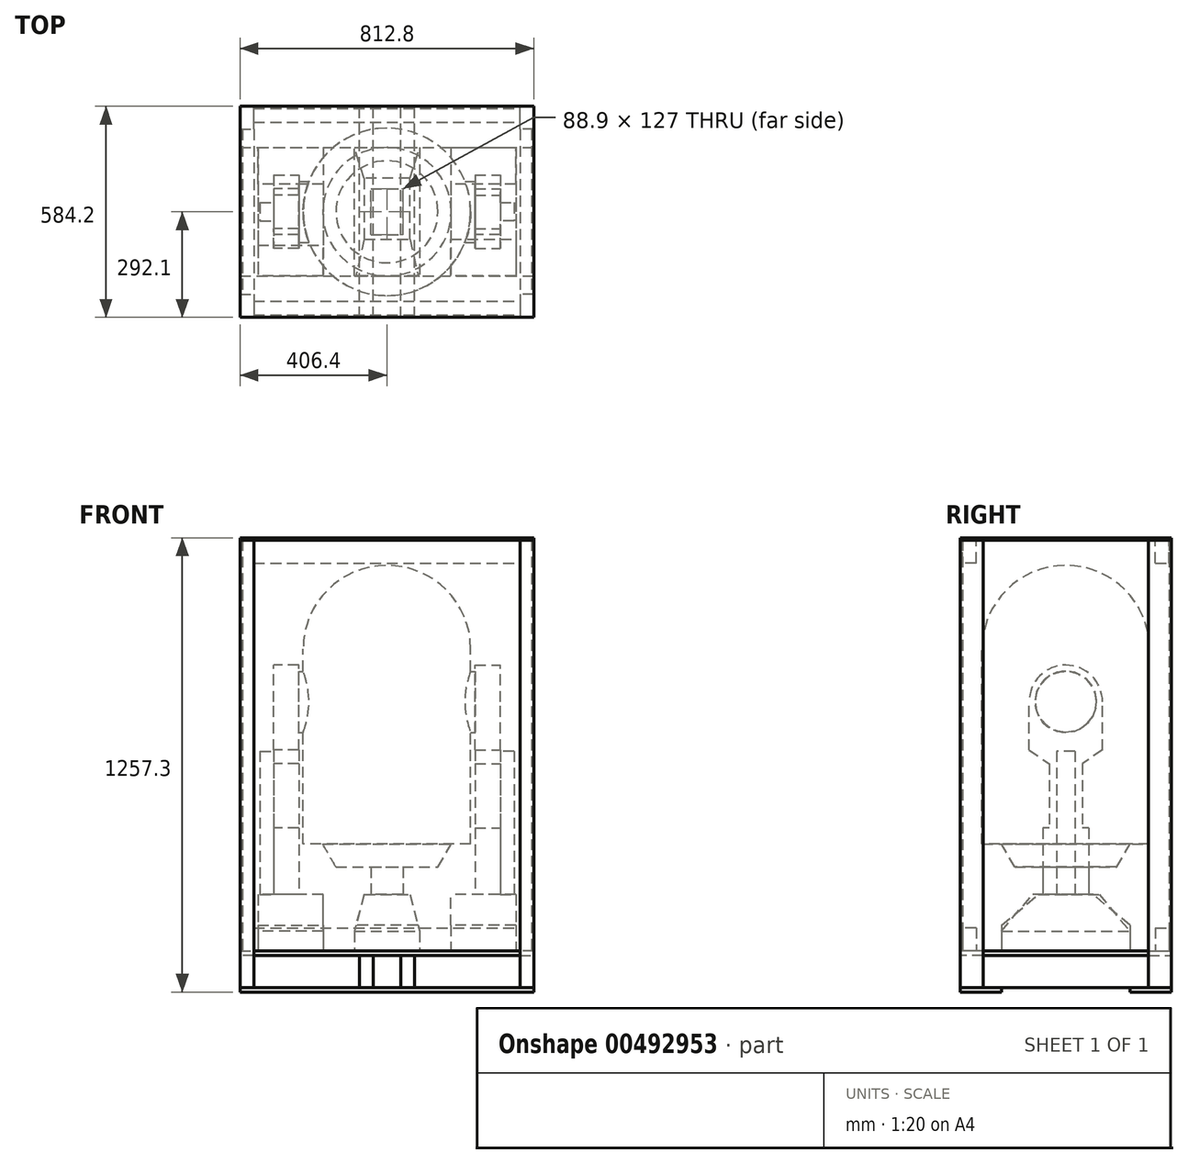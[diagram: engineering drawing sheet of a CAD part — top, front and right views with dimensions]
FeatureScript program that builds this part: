
annotation { "Feature Type Name" : "Feature", "Feature Type Description" : "" }
export const myFeature = defineFeature(function(context is Context, id is Id, definition is map)
    precondition{}
    {
        {
            var Q0;
            Q0=qCreatedBy(makeId("Top.planeOp"),FACE);
            var sketch = newSketch(context, id + "F0", { "sketchPlane" : qUnion([Q0])});
            skCircle(sketch, "E0", {"center": v(0, 0) * mm, "radius": 231.78 * mm});
            skLineSegment(sketch, "E1.bottom", {"start": v(243.68, 84.58) * mm, "end": v(215.8, 84.58) * mm});
            skLineSegment(sketch, "E1.top", {"start": v(243.68, -84.58) * mm, "end": v(215.8, -84.58) * mm});
            skLineSegment(sketch, "E1.left", {"start": v(243.68, 84.58) * mm, "end": v(243.68, -84.58) * mm});
            skLineSegment(sketch, "E1.right", {"start": v(-243.68, 84.58) * mm, "end": v(-243.68, -84.58) * mm});
            skLineSegment(sketch, "E2.bottom", {"start": v(313.53, 101.6) * mm, "end": v(243.68, 101.6) * mm});
            skLineSegment(sketch, "E2.top", {"start": v(313.53, -101.6) * mm, "end": v(243.68, -101.6) * mm});
            skLineSegment(sketch, "E2.left", {"start": v(313.53, 101.6) * mm, "end": v(313.53, -101.6) * mm});
            skLineSegment(sketch, "E2.right", {"start": v(243.68, 101.6) * mm, "end": v(243.68, -101.6) * mm});
            skPoint(sketch, "E2.middle", {"position": v(278.6, 0) * mm});
            skLineSegment(sketch, "E3.bottom", {"start": v(338.93, -50.8) * mm, "end": v(313.53, -50.8) * mm});
            skLineSegment(sketch, "E3.top", {"start": v(338.93, 50.8) * mm, "end": v(313.53, 50.8) * mm});
            skLineSegment(sketch, "E3.left", {"start": v(338.93, -50.8) * mm, "end": v(338.93, 50.8) * mm});
            skLineSegment(sketch, "E3.right", {"start": v(313.53, -50.8) * mm, "end": v(313.53, 50.8) * mm});
            skPoint(sketch, "E3.middle", {"position": v(326.23, 0) * mm});
            skLineSegment(sketch, "E4.trimOffspring", {"start": v(-215.8, 84.58) * mm, "end": v(-243.68, 84.58) * mm});
            skLineSegment(sketch, "E5.trimOffspring", {"start": v(-215.8, -84.58) * mm, "end": v(-243.68, -84.58) * mm});
            skLineSegment(sketch, "E6.MirrorCS", {"start": v(-243.68, 101.6) * mm, "end": v(-243.68, -101.6) * mm});
            skLineSegment(sketch, "E7.MirrorCS", {"start": v(-313.53, 101.6) * mm, "end": v(-243.68, 101.6) * mm});
            skLineSegment(sketch, "E8.MirrorCS", {"start": v(-313.53, -101.6) * mm, "end": v(-243.68, -101.6) * mm});
            skLineSegment(sketch, "E9.MirrorCS", {"start": v(-313.53, 101.6) * mm, "end": v(-313.53, -101.6) * mm});
            skLineSegment(sketch, "E10.MirrorCS", {"start": v(-338.93, -50.8) * mm, "end": v(-313.53, -50.8) * mm});
            skLineSegment(sketch, "E11.MirrorCS", {"start": v(-338.93, -50.8) * mm, "end": v(-338.93, 50.8) * mm});
            skLineSegment(sketch, "E12.MirrorCS", {"start": v(-338.93, 50.8) * mm, "end": v(-313.53, 50.8) * mm});
            skLineSegment(sketch, "E13", {"start": v(0, 0) * mm, "end": v(0, 231.78) * mm});
            skLineSegment(sketch, "E14", {"start": v(0, 0) * mm, "end": v(0, -231.78) * mm});
            skLineSegment(sketch, "E15", {"start": v(313.53, 0) * mm, "end": v(243.68, 0) * mm});
            skLineSegment(sketch, "E16", {"start": v(-243.68, 0) * mm, "end": v(-313.53, 0) * mm});
            skSolve(sketch);
        }
        {
            var Q0;
            {var subQ0=sQuery(id+"F0.wireOp",EDGE,"E0");var subQ1=makeQuery(id+"F0.imprint","INTERSECT",VERTEX,{"derivedFrom":[subQ0,sQuery(id+"F0.wireOp",EDGE,"E1.bottom")]});Q0=makeQuery(id+"F0.imprint","IMPRINT",FACE,{"disambiguationData":[TD([[makeQuery(id+"F0.imprint","IMPRINT",EDGE,{"disambiguationData":[TD([[subQ1,-1.0]])],"derivedFrom":subQ0}),1.0]])]});}
            var Q1;
            {var subQ3=sQuery(id+"F0.wireOp",EDGE,"E13");Q1=makeQuery(id+"F0.imprint","IMPRINT",FACE,{"disambiguationData":[TD([[makeQuery(id+"F0.imprint","IMPRINT",EDGE,{"derivedFrom":subQ3}),1.0]])]});}
            extrude(context, id + "F1", {"entities" : qUnion([Q0, Q1]), "oppositeDirection" : true, "depth" : 539.75 * mm});
        }
        {
            var Q0;
            {var subQ0=sQuery(id+"F0.wireOp",EDGE,"E13");Q0=makeQuery(id+"F0.imprint","IMPRINT",FACE,{"disambiguationData":[TD([[makeQuery(id+"F0.imprint","IMPRINT",EDGE,{"derivedFrom":subQ0}),-1.0]])]});}
            var Q1;
            Q1=sQuery(id+"F0.wireOp",EDGE,"E14");
            revolve(context, id + "F2", {"operationType" : NewBodyOperationType.ADD, "entities" : qUnion([Q0]), "axis" : qUnion([Q1]), "revolveType" : RevolveType.ONE_DIRECTION, "angle" : 180 * degree});
        }
        {
            var Q0;
            {var subQ2=sQuery(id+"F0.wireOp",EDGE,"E2.top");Q0=makeQuery(id+"F0.imprint","IMPRINT",FACE,{"disambiguationData":[TD([[makeQuery(id+"F0.imprint","IMPRINT",EDGE,{"derivedFrom":subQ2}),-1.0]])]});}
            var Q1;
            {var subQ2=sQuery(id+"F0.wireOp",EDGE,"E2.bottom");Q1=makeQuery(id+"F0.imprint","IMPRINT",FACE,{"disambiguationData":[TD([[makeQuery(id+"F0.imprint","IMPRINT",EDGE,{"derivedFrom":subQ2}),1.0]])]});}
            extrude(context, id + "F3", {"entities" : qUnion([Q0, Q1]), "oppositeDirection" : true, "depth" : 714.38 * mm, "hasSecondDirection" : true, "secondDirectionOppositeDirection" : true, "secondDirectionDepth" : 146.05 * mm});
        }
        {
            var Q0;
            Q0=makeQuery(id+"F3.opExtrude","CAP_FACE",FACE,{"disambiguationData":[OSD([sQuery(id+"F0.wireOp",EDGE,"E2.bottom"),sQuery(id+"F0.wireOp",EDGE,"E2.top"),sQuery(id+"F0.wireOp",EDGE,"E2.left"),sQuery(id+"F0.wireOp",EDGE,"E2.right"),sQuery(id+"F0.wireOp",EDGE,"E3.right")])],"isStart":true});
            var sketch = newSketch(context, id + "F4", { "sketchPlane" : qUnion([Q0])});
            skLineSegment(sketch, "E17", {"start": v(313.53, 0) * mm, "end": v(243.68, 0) * mm});
            skSolve(sketch);
        }
        {
            var Q0;
            {var subQ0=sQuery(id+"F4.wireOp",EDGE,"E17");Q0=makeQuery(id+"F4.imprint","IMPRINT",FACE,{"disambiguationData":[TD([[makeQuery(id+"F4.imprint","IMPRINT",EDGE,{"derivedFrom":subQ0}),1.0]])]});}
            var Q1;
            Q1=sQuery(id+"F4.wireOp",EDGE,"E17");
            revolve(context, id + "F5", {"operationType" : NewBodyOperationType.ADD, "entities" : qUnion([Q0]), "axis" : qUnion([Q1]), "revolveType" : RevolveType.FULL});
        }
        {
            var Q0;
            {var subQ0=sQuery(id+"F0.wireOp",EDGE,"E3.right");var subQ1=sQuery(id+"F0.wireOp",EDGE,"E2.left");Q0=makeQuery(id+"F5.boolean.opBoolean","MERGE",FACE,{"derivedFrom":[makeQuery(id+"F3.opExtrude","SWEPT_FACE",FACE,{"disambiguationData":[OSD([subQ1,subQ0])]}),makeQuery(id+"F5.opRevolve","SWEPT_FACE",FACE,{"disambiguationData":[OSD([subQ1,subQ0])]})]});}
            var sketch = newSketch(context, id + "F6", { "sketchPlane" : qUnion([Q0])});
            skCircle(sketch, "E18", {"center": v(0, -146.05) * mm, "radius": 84.58 * mm});
            skLineSegment(sketch, "E19.bottom", {"start": v(46.04, -317.5) * mm, "end": v(-46.04, -317.5) * mm, "construction": true});
            skLineSegment(sketch, "E19.left", {"start": v(46.04, -317.5) * mm, "end": v(46.04, -495.3) * mm});
            skLineSegment(sketch, "E19.right", {"start": v(-46.04, -317.5) * mm, "end": v(-46.04, -495.3) * mm});
            skPoint(sketch, "E19.middle", {"position": v(0, -406.4) * mm});
            skLineSegment(sketch, "E20", {"start": v(-101.6, -279.4) * mm, "end": v(-46.04, -317.5) * mm});
            skLineSegment(sketch, "E21", {"start": v(101.6, -279.4) * mm, "end": v(46.04, -317.5) * mm});
            skLineSegment(sketch, "E22.bottom", {"start": v(63.5, -495.3) * mm, "end": v(46.04, -495.3) * mm});
            skLineSegment(sketch, "E22.top", {"start": v(63.5, -714.38) * mm, "end": v(-63.5, -714.38) * mm});
            skLineSegment(sketch, "E22.left", {"start": v(63.5, -495.3) * mm, "end": v(63.5, -714.38) * mm});
            skLineSegment(sketch, "E22.right", {"start": v(-63.5, -495.3) * mm, "end": v(-63.5, -714.38) * mm});
            skPoint(sketch, "E22.middle", {"position": v(0, -604.84) * mm});
            skLineSegment(sketch, "E23.trimOffspring", {"start": v(-46.04, -495.3) * mm, "end": v(-63.5, -495.3) * mm});
            skSolve(sketch);
        }
        {
            var Q0;
            Q0=makeQuery(id+"F6.imprint","IMPRINT",FACE,{"disambiguationData":[TD([[makeQuery(id+"F6.imprint","IMPRINT",EDGE,{"derivedFrom":sQuery(id+"F6.wireOp",EDGE,"E19.left")}),1.0]])]});
            var Q1;
            Q1=makeQuery(id+"F6.imprint","IMPRINT",FACE,{"disambiguationData":[TD([[makeQuery(id+"F6.imprint","IMPRINT",EDGE,{"derivedFrom":sQuery(id+"F6.wireOp",EDGE,"E19.right")}),-1.0]])]});
            var Q2;
            {var subQ0=sQuery(id+"F0.wireOp",EDGE,"E2.right");Q2=makeQuery(id+"F5.boolean.opBoolean","MERGE",FACE,{"derivedFrom":[makeQuery(id+"F3.opExtrude","SWEPT_FACE",FACE,{"disambiguationData":[OSD([subQ0])]}),makeQuery(id+"F5.opRevolve","SWEPT_FACE",FACE,{"disambiguationData":[OSD([subQ0])]})]});}
            extrude(context, id + "F7", {"entities" : qUnion([Q0, Q1]), "operationType" : NewBodyOperationType.REMOVE, "endBound" : BoundingType.UP_TO_SURFACE, "oppositeDirection" : true, "endBoundEntityFace" : qUnion([Q2]), "depth" : 25.4 * mm});
        }
        {
            var Q0;
            Q0=makeQuery(id+"F6.imprint","IMPRINT",FACE,{"disambiguationData":[TD([[makeQuery(id+"F6.imprint","IMPRINT",EDGE,{"derivedFrom":sQuery(id+"F6.wireOp",EDGE,"E18")}),-1.0]])]});
            var sketch = newSketch(context, id + "F8", { "sketchPlane" : qUnion([Q0])});
            skLineSegment(sketch, "E24.bottom", {"start": v(25.4, -282.58) * mm, "end": v(-25.4, -282.58) * mm});
            skLineSegment(sketch, "E24.top", {"start": v(25.4, -714.38) * mm, "end": v(-25.4, -714.38) * mm});
            skLineSegment(sketch, "E24.left", {"start": v(25.4, -282.58) * mm, "end": v(25.4, -714.38) * mm});
            skLineSegment(sketch, "E24.right", {"start": v(-25.4, -282.58) * mm, "end": v(-25.4, -714.38) * mm});
            skPoint(sketch, "E24.middle", {"position": v(0, -498.48) * mm});
            skSolve(sketch);
        }
        {
            var Q0;
            Q0=makeQuery(id+"F8.imprint","IMPRINT",FACE,{"disambiguationData":[TD([[makeQuery(id+"F8.imprint","IMPRINT",EDGE,{"derivedFrom":sQuery(id+"F8.wireOp",EDGE,"E24.bottom")}),1.0]])]});
            extrude(context, id + "F9", {"entities" : qUnion([Q0]), "operationType" : NewBodyOperationType.ADD, "depth" : 38.1 * mm});
        }
        {
            var Q0;
            Q0=makeQuery(id+"F3.opExtrude","SWEPT_BODY",BODY,{"disambiguationData":[OSD([sQuery(id+"F0.wireOp",EDGE,"E2.bottom"),sQuery(id+"F0.wireOp",EDGE,"E2.top"),sQuery(id+"F0.wireOp",EDGE,"E2.left"),sQuery(id+"F0.wireOp",EDGE,"E2.right"),sQuery(id+"F0.wireOp",EDGE,"E3.right")])]});
            var Q1;
            Q1=qCreatedBy(makeId("Right.planeOp"),FACE);
            mirror(context, id + "F10", {"entities" : qUnion([Q0]), "mirrorPlane" : qUnion([Q1])});
        }
        {
            var Q0;
            Q0=makeQuery(id+"F6.imprint","IMPRINT",FACE,{"disambiguationData":[TD([[makeQuery(id+"F6.imprint","IMPRINT",EDGE,{"derivedFrom":sQuery(id+"F6.wireOp",EDGE,"E18")}),1.0]])]});
            var Q1;
            Q1=sQuery(id+"F6.wireOp",EDGE,"E18");
            var Q2;
            {var subQ0=sQuery(id+"F0.wireOp",EDGE,"E3.right");var subQ1=sQuery(id+"F0.wireOp",EDGE,"E2.left");Q2=makeQuery(id+"F10.opPattern","COPY",FACE,{"derivedFrom":makeQuery(id+"F5.boolean.opBoolean","MERGE",FACE,{"derivedFrom":[makeQuery(id+"F3.opExtrude","SWEPT_FACE",FACE,{"disambiguationData":[OSD([subQ1,subQ0])]}),makeQuery(id+"F5.opRevolve","SWEPT_FACE",FACE,{"disambiguationData":[OSD([subQ1,subQ0])]})]}),"instanceName":"1"});}
            extrude(context, id + "F11", {"entities" : qUnion([Q0]), "operationType" : NewBodyOperationType.ADD, "surfaceEntities" : qUnion([Q1]), "endBound" : BoundingType.UP_TO_SURFACE, "oppositeDirection" : true, "endBoundEntityFace" : qUnion([Q2]), "depth" : 25.4 * mm});
        }
        {
            var Q0;
            Q0=makeQuery(id+"F1.opExtrude","CAP_FACE",FACE,{"disambiguationData":[OSD([sQuery(id+"F0.wireOp",EDGE,"E0")])],"isStart":false});
            var sketch = newSketch(context, id + "F12", { "sketchPlane" : qUnion([Q0])});
            skCircle(sketch, "E25", {"center": v(0, 0) * mm, "radius": 177.8 * mm});
            skSolve(sketch);
        }
        {
            var Q0;
            Q0=makeQuery(id+"F12.imprint","IMPRINT",FACE,{"disambiguationData":[TD([[makeQuery(id+"F12.imprint","IMPRINT",EDGE,{"derivedFrom":sQuery(id+"F12.wireOp",EDGE,"E25")}),1.0]])]});
            extrude(context, id + "F13", {"entities" : qUnion([Q0]), "operationType" : NewBodyOperationType.ADD, "depth" : 63.5 * mm});
        }
        {
            var Q0;
            Q0=makeQuery(id+"F13.opExtrude","CAP_EDGE",EDGE,{"disambiguationData":[OSD([sQuery(id+"F12.wireOp",EDGE,"E25")])],"isStart":false});
            chamfer(context, id + "F14", {"entities" : qUnion([Q0]), "chamferType" : ChamferType.OFFSET_ANGLE, "width" : 63.5 * mm, "oppositeDirection" : true, "angle" : 30 * degree, "tangentPropagation" : true});
        }
        {
            var Q0;
            Q0=qCreatedBy(makeId("Top.planeOp"),FACE);
            cPlane(context, id + "F15", {"entities" : qUnion([Q0]), "cplaneType" : CPlaneType.OFFSET, "offset" : 835.02 * mm, "oppositeDirection" : true, "width" : 152.4 * mm, "height" : 152.4 * mm});
        }
        {
            var Q0;
            Q0=qCreatedBy(id+"F15.planeOp",FACE);
            var sketch = newSketch(context, id + "F16", { "sketchPlane" : qUnion([Q0])});
            skLineSegment(sketch, "E26.bottom", {"start": v(-90.49, 177.8) * mm, "end": v(90.49, 177.8) * mm});
            skLineSegment(sketch, "E26.top", {"start": v(-90.49, -177.8) * mm, "end": v(90.49, -177.8) * mm});
            skLineSegment(sketch, "E26.left", {"start": v(-90.49, 177.8) * mm, "end": v(-90.49, -177.8) * mm});
            skLineSegment(sketch, "E26.right", {"start": v(90.49, 177.8) * mm, "end": v(90.49, -177.8) * mm});
            skPoint(sketch, "E26.middle", {"position": v(0, 0) * mm});
            skLineSegment(sketch, "E27.1.0.0", {"start": v(176.21, -177.8) * mm, "end": v(357.19, -177.8) * mm});
            skLineSegment(sketch, "E27.1.0.1", {"start": v(176.21, 177.8) * mm, "end": v(176.21, -177.8) * mm});
            skLineSegment(sketch, "E27.1.0.2", {"start": v(357.19, 177.8) * mm, "end": v(357.19, -177.8) * mm});
            skLineSegment(sketch, "E27.1.0.3", {"start": v(176.21, 177.8) * mm, "end": v(357.19, 177.8) * mm});
            skLineSegment(sketch, "E27.direction1", {"start": v(-90.49, -177.8) * mm, "end": v(176.21, -177.8) * mm, "construction": true});
            skLineSegment(sketch, "E28", {"start": v(266.7, -177.8) * mm, "end": v(266.7, 177.8) * mm, "construction": true});
            skLineSegment(sketch, "E29", {"start": v(0, -177.8) * mm, "end": v(0, 177.8) * mm, "construction": true});
            skLineSegment(sketch, "E30.MirrorCS", {"start": v(-176.21, 177.8) * mm, "end": v(-176.21, -177.8) * mm});
            skLineSegment(sketch, "E31.MirrorCS", {"start": v(-176.21, -177.8) * mm, "end": v(-357.19, -177.8) * mm});
            skLineSegment(sketch, "E32.MirrorCS", {"start": v(-357.19, 177.8) * mm, "end": v(-357.19, -177.8) * mm});
            skLineSegment(sketch, "E33.MirrorCS", {"start": v(-176.21, 177.8) * mm, "end": v(-357.19, 177.8) * mm});
            skSolve(sketch);
        }
        {
            var Q0;
            Q0=makeQuery(id+"F16.imprint","IMPRINT",FACE,{"disambiguationData":[TD([[makeQuery(id+"F16.imprint","IMPRINT",EDGE,{"derivedFrom":sQuery(id+"F16.wireOp",EDGE,"E30.MirrorCS")}),-1.0]])]});
            var Q1;
            Q1=makeQuery(id+"F16.imprint","IMPRINT",FACE,{"disambiguationData":[TD([[makeQuery(id+"F16.imprint","IMPRINT",EDGE,{"derivedFrom":sQuery(id+"F16.wireOp",EDGE,"E26.bottom")}),-1.0]])]});
            var Q2;
            Q2=makeQuery(id+"F16.imprint","IMPRINT",FACE,{"disambiguationData":[TD([[makeQuery(id+"F16.imprint","IMPRINT",EDGE,{"derivedFrom":sQuery(id+"F16.wireOp",EDGE,"E27.1.0.0")}),1.0]])]});
            extrude(context, id + "F17", {"entities" : qUnion([Q0, Q1, Q2]), "operationType" : NewBodyOperationType.ADD, "depth" : 155.57 * mm});
        }
        {
            var Q0;
            Q0=makeQuery(id+"F17.opExtrude","CAP_FACE",FACE,{"disambiguationData":[OSD([sQuery(id+"F16.wireOp",EDGE,"E26.bottom"),sQuery(id+"F16.wireOp",EDGE,"E26.top"),sQuery(id+"F16.wireOp",EDGE,"E26.left"),sQuery(id+"F16.wireOp",EDGE,"E26.right")])],"isStart":false});
            var sketch = newSketch(context, id + "F18", { "sketchPlane" : qUnion([Q0])});
            skLineSegment(sketch, "E34.bottom", {"start": v(44.45, 63.5) * mm, "end": v(-44.45, 63.5) * mm});
            skLineSegment(sketch, "E34.top", {"start": v(44.45, -63.5) * mm, "end": v(-44.45, -63.5) * mm});
            skLineSegment(sketch, "E34.left", {"start": v(44.45, 63.5) * mm, "end": v(44.45, -63.5) * mm});
            skLineSegment(sketch, "E34.right", {"start": v(-44.45, 63.5) * mm, "end": v(-44.45, -63.5) * mm});
            skPoint(sketch, "E34.middle", {"position": v(0, 0) * mm});
            skSolve(sketch);
        }
        {
            var Q0;
            Q0=makeQuery(id+"F18.imprint","IMPRINT",FACE,{"disambiguationData":[TD([[makeQuery(id+"F18.imprint","IMPRINT",EDGE,{"derivedFrom":sQuery(id+"F18.wireOp",EDGE,"E34.bottom")}),1.0]])]});
            var Q1;
            Q1=makeQuery(id+"F13.opExtrude","CAP_FACE",FACE,{"disambiguationData":[OSD([sQuery(id+"F12.wireOp",EDGE,"E25")])],"isStart":false});
            extrude(context, id + "F19", {"entities" : qUnion([Q0]), "operationType" : NewBodyOperationType.ADD, "endBound" : BoundingType.UP_TO_SURFACE, "endBoundEntityFace" : qUnion([Q1]), "depth" : 25.4 * mm});
        }
        {
            var Q0;
            Q0=makeQuery(id+"F17.opExtrude","CAP_EDGE",EDGE,{"disambiguationData":[OSD([sQuery(id+"F16.wireOp",EDGE,"E27.1.0.0")])],"isStart":false});
            var Q1;
            Q1=makeQuery(id+"F17.opExtrude","CAP_EDGE",EDGE,{"disambiguationData":[OSD([sQuery(id+"F16.wireOp",EDGE,"E31.MirrorCS")])],"isStart":false});
            var Q2;
            Q2=makeQuery(id+"F17.opExtrude","CAP_EDGE",EDGE,{"disambiguationData":[OSD([sQuery(id+"F16.wireOp",EDGE,"E33.MirrorCS")])],"isStart":false});
            var Q3;
            Q3=makeQuery(id+"F17.opExtrude","CAP_EDGE",EDGE,{"disambiguationData":[OSD([sQuery(id+"F16.wireOp",EDGE,"E27.1.0.3")])],"isStart":false});
            var Q4;
            Q4=makeQuery(id+"F17.opExtrude","CAP_EDGE",EDGE,{"disambiguationData":[OSD([sQuery(id+"F16.wireOp",EDGE,"E26.bottom")])],"isStart":false});
            var Q5;
            Q5=makeQuery(id+"F17.opExtrude","CAP_EDGE",EDGE,{"disambiguationData":[OSD([sQuery(id+"F16.wireOp",EDGE,"E26.top")])],"isStart":false});
            chamfer(context, id + "F20", {"entities" : qUnion([Q0, Q1, Q2, Q3, Q4, Q5]), "chamferType" : ChamferType.OFFSET_ANGLE, "width" : 101.6 * mm, "oppositeDirection" : false, "angle" : 40 * degree, "tangentPropagation" : true});
        }
        {
            var Q0;
            Q0=makeQuery(id+"F17.opExtrude","CAP_EDGE",EDGE,{"disambiguationData":[OSD([sQuery(id+"F16.wireOp",EDGE,"E26.left")])],"isStart":false});
            var Q1;
            Q1=makeQuery(id+"F17.opExtrude","CAP_EDGE",EDGE,{"disambiguationData":[OSD([sQuery(id+"F16.wireOp",EDGE,"E26.right")])],"isStart":false});
            chamfer(context, id + "F21", {"entities" : qUnion([Q0, Q1]), "chamferType" : ChamferType.OFFSET_ANGLE, "width" : 101.6 * mm, "oppositeDirection" : true, "angle" : 15 * degree});
        }
        {
            var Q0;
            Q0=qCreatedBy(id+"F15.planeOp",FACE);
            var sketch = newSketch(context, id + "F22", { "sketchPlane" : qUnion([Q0])});
            skLineSegment(sketch, "E35.bottom", {"start": v(406.4, -292.1) * mm, "end": v(-406.4, -292.1) * mm});
            skLineSegment(sketch, "E35.top", {"start": v(406.4, 292.1) * mm, "end": v(-406.4, 292.1) * mm});
            skLineSegment(sketch, "E35.left", {"start": v(406.4, -292.1) * mm, "end": v(406.4, 292.1) * mm});
            skLineSegment(sketch, "E35.right", {"start": v(-406.4, -292.1) * mm, "end": v(-406.4, 292.1) * mm});
            skPoint(sketch, "E35.middle", {"position": v(0, 0) * mm});
            skLineSegment(sketch, "E36", {"start": v(-406.4, -228.6) * mm, "end": v(-368.3, -228.6) * mm});
            skLineSegment(sketch, "E37", {"start": v(-368.3, -228.6) * mm, "end": v(-368.3, -292.1) * mm});
            skLineSegment(sketch, "E38", {"start": v(0, -292.1) * mm, "end": v(0, 292.1) * mm, "construction": true});
            skLineSegment(sketch, "E39", {"start": v(406.4, 0) * mm, "end": v(-406.4, 0) * mm, "construction": true});
            skLineSegment(sketch, "E40.MirrorCS", {"start": v(368.3, -228.6) * mm, "end": v(368.3, -292.1) * mm});
            skLineSegment(sketch, "E41.MirrorCS", {"start": v(406.4, -228.6) * mm, "end": v(368.3, -228.6) * mm});
            skLineSegment(sketch, "E42.MirrorCS", {"start": v(-406.4, 228.6) * mm, "end": v(-368.3, 228.6) * mm});
            skLineSegment(sketch, "E43.MirrorCS", {"start": v(-368.3, 228.6) * mm, "end": v(-368.3, 292.1) * mm});
            skLineSegment(sketch, "E44.MirrorCS", {"start": v(406.4, 228.6) * mm, "end": v(368.3, 228.6) * mm});
            skLineSegment(sketch, "E45.MirrorCS", {"start": v(368.3, 228.6) * mm, "end": v(368.3, 292.1) * mm});
            skLineSegment(sketch, "E46", {"start": v(368.3, 285.75) * mm, "end": v(-368.3, 285.75) * mm});
            skLineSegment(sketch, "E47", {"start": v(-400.05, 228.6) * mm, "end": v(-400.05, -228.6) * mm});
            skLineSegment(sketch, "E48", {"start": v(-135.56, 292.1) * mm, "end": v(-135.56, 285.75) * mm, "construction": true});
            skLineSegment(sketch, "E49", {"start": v(-400.05, 178.52) * mm, "end": v(-406.4, 178.52) * mm, "construction": true});
            skLineSegment(sketch, "E50.MirrorCS", {"start": v(368.3, -285.75) * mm, "end": v(-368.3, -285.75) * mm});
            skLineSegment(sketch, "E51.MirrorCS", {"start": v(400.05, 228.6) * mm, "end": v(400.05, -228.6) * mm});
            skSolve(sketch);
        }
        {
            var Q0;
            {var subQ4=sQuery(id+"F22.wireOp",EDGE,"E44.MirrorCS");Q0=makeQuery(id+"F22.imprint","IMPRINT",FACE,{"disambiguationData":[TD([[makeQuery(id+"F22.imprint","IMPRINT",EDGE,{"derivedFrom":subQ4}),-1.0]])]});}
            var Q1;
            {var subQ3=sQuery(id+"F22.wireOp",EDGE,"E40.MirrorCS");Q1=makeQuery(id+"F22.imprint","IMPRINT",FACE,{"disambiguationData":[TD([[makeQuery(id+"F22.imprint","IMPRINT",EDGE,{"derivedFrom":subQ3}),1.0]])]});}
            var Q2;
            {var subQ4=sQuery(id+"F22.wireOp",EDGE,"E42.MirrorCS");Q2=makeQuery(id+"F22.imprint","IMPRINT",FACE,{"disambiguationData":[TD([[makeQuery(id+"F22.imprint","IMPRINT",EDGE,{"derivedFrom":subQ4}),1.0]])]});}
            var Q3;
            {var subQ4=sQuery(id+"F22.wireOp",EDGE,"E36");Q3=makeQuery(id+"F22.imprint","IMPRINT",FACE,{"disambiguationData":[TD([[makeQuery(id+"F22.imprint","IMPRINT",EDGE,{"derivedFrom":subQ4}),-1.0]])]});}
            extrude(context, id + "F23", {"entities" : qUnion([Q0, Q1, Q2, Q3]), "depth" : 1136.65 * mm, "hasSecondDirection" : true, "secondDirectionOppositeDirection" : true, "secondDirectionDepth" : 101.6 * mm});
        }
        {
            var Q0;
            {var subQ4=sQuery(id+"F22.wireOp",EDGE,"E36");Q0=makeQuery(id+"F22.imprint","IMPRINT",FACE,{"disambiguationData":[TD([[makeQuery(id+"F22.imprint","IMPRINT",EDGE,{"derivedFrom":subQ4}),1.0]])]});}
            var Q1;
            {var subQ1=sQuery(id+"F22.wireOp",EDGE,"E46");Q1=makeQuery(id+"F22.imprint","IMPRINT",FACE,{"disambiguationData":[TD([[makeQuery(id+"F22.imprint","IMPRINT",EDGE,{"derivedFrom":subQ1}),1.0]])]});}
            var Q2;
            {var subQ5=sQuery(id+"F22.wireOp",EDGE,"E46");Q2=makeQuery(id+"F22.imprint","IMPRINT",FACE,{"disambiguationData":[TD([[makeQuery(id+"F22.imprint","IMPRINT",EDGE,{"derivedFrom":subQ5}),-1.0]])]});}
            var Q3;
            {var subQ5=sQuery(id+"F22.wireOp",EDGE,"E50.MirrorCS");Q3=makeQuery(id+"F22.imprint","IMPRINT",FACE,{"disambiguationData":[TD([[makeQuery(id+"F22.imprint","IMPRINT",EDGE,{"derivedFrom":subQ5}),1.0]])]});}
            var Q4;
            {var subQ5=sQuery(id+"F22.wireOp",EDGE,"E51.MirrorCS");Q4=makeQuery(id+"F22.imprint","IMPRINT",FACE,{"disambiguationData":[TD([[makeQuery(id+"F22.imprint","IMPRINT",EDGE,{"derivedFrom":subQ5}),1.0]])]});}
            extrude(context, id + "F24", {"entities" : qUnion([Q0, Q1, Q2, Q3, Q4]), "oppositeDirection" : true, "depth" : 12.7 * mm});
        }
        {
            var Q0;
            {var subQ5=sQuery(id+"F22.wireOp",EDGE,"E46");Q0=makeQuery(id+"F22.imprint","IMPRINT",FACE,{"disambiguationData":[TD([[makeQuery(id+"F22.imprint","IMPRINT",EDGE,{"derivedFrom":subQ5}),-1.0]])]});}
            var Q1;
            {var subQ5=sQuery(id+"F22.wireOp",EDGE,"E51.MirrorCS");Q1=makeQuery(id+"F22.imprint","IMPRINT",FACE,{"disambiguationData":[TD([[makeQuery(id+"F22.imprint","IMPRINT",EDGE,{"derivedFrom":subQ5}),1.0]])]});}
            var Q2;
            {var subQ5=sQuery(id+"F22.wireOp",EDGE,"E50.MirrorCS");Q2=makeQuery(id+"F22.imprint","IMPRINT",FACE,{"disambiguationData":[TD([[makeQuery(id+"F22.imprint","IMPRINT",EDGE,{"derivedFrom":subQ5}),1.0]])]});}
            var Q3;
            {var subQ5=sQuery(id+"F22.wireOp",EDGE,"E47");Q3=makeQuery(id+"F22.imprint","IMPRINT",FACE,{"disambiguationData":[TD([[makeQuery(id+"F22.imprint","IMPRINT",EDGE,{"derivedFrom":subQ5}),-1.0]])]});}
            var Q4;
            Q4=makeQuery(id+"F23.opExtrude","CAP_FACE",FACE,{"disambiguationData":[OSD([sQuery(id+"F22.wireOp",EDGE,"E35.top"),sQuery(id+"F22.wireOp",EDGE,"E35.left"),sQuery(id+"F22.wireOp",EDGE,"E44.MirrorCS"),sQuery(id+"F22.wireOp",EDGE,"E45.MirrorCS")])],"isStart":false});
            extrude(context, id + "F25", {"entities" : qUnion([Q0, Q1, Q2, Q3]), "endBound" : BoundingType.UP_TO_SURFACE, "endBoundEntityFace" : qUnion([Q4]), "depth" : 25.4 * mm});
        }
        {
            var Q0;
            Q0=makeQuery(id+"F23.opExtrude","SWEPT_FACE",FACE,{"disambiguationData":[OSD([sQuery(id+"F22.wireOp",EDGE,"E41.MirrorCS")])]});
            var sketch = newSketch(context, id + "F26", { "sketchPlane" : qUnion([Q0])});
            skLineSegment(sketch, "E52", {"start": v(-406.4, -847.73) * mm, "end": v(-368.3, -847.73) * mm});
            skLineSegment(sketch, "E53", {"start": v(-406.4, -936.63) * mm, "end": v(-368.3, -936.63) * mm});
            skSolve(sketch);
        }
        {
            var Q0;
            {var subQ0=sQuery(id+"F26.wireOp",EDGE,"E52");Q0=makeQuery(id+"F26.imprint","IMPRINT",FACE,{"disambiguationData":[TD([[makeQuery(id+"F26.imprint","IMPRINT",EDGE,{"derivedFrom":subQ0}),-1.0]])]});}
            var Q1;
            Q1=makeQuery(id+"F23.opExtrude","SWEPT_FACE",FACE,{"disambiguationData":[OSD([sQuery(id+"F22.wireOp",EDGE,"E44.MirrorCS")])]});
            extrude(context, id + "F27", {"entities" : qUnion([Q0]), "endBound" : BoundingType.UP_TO_SURFACE, "endBoundEntityFace" : qUnion([Q1]), "depth" : 25.4 * mm});
        }
        {
            var Q0;
            Q0=makeQuery(id+"F27.opExtrude","SWEPT_BODY",BODY,{"disambiguationData":[OSD([sQuery(id+"F22.wireOp",EDGE,"E35.left"),sQuery(id+"F22.wireOp",EDGE,"E40.MirrorCS"),sQuery(id+"F22.wireOp",EDGE,"E41.MirrorCS"),sQuery(id+"F26.wireOp",EDGE,"E52"),sQuery(id+"F26.wireOp",EDGE,"E53")])]});
            var Q1;
            Q1=qCreatedBy(makeId("Right.planeOp"),FACE);
            mirror(context, id + "F28", {"entities" : qUnion([Q0]), "mirrorPlane" : qUnion([Q1])});
        }
        {
            var Q0;
            Q0=makeQuery(id+"F23.opExtrude","CAP_FACE",FACE,{"disambiguationData":[OSD([sQuery(id+"F22.wireOp",EDGE,"E35.top"),sQuery(id+"F22.wireOp",EDGE,"E35.left"),sQuery(id+"F22.wireOp",EDGE,"E44.MirrorCS"),sQuery(id+"F22.wireOp",EDGE,"E45.MirrorCS")])],"isStart":false});
            var sketch = newSketch(context, id + "F29", { "sketchPlane" : qUnion([Q0])});
            skLineSegment(sketch, "E54.bottom", {"start": v(406.4, 292.1) * mm, "end": v(-406.4, 292.1) * mm});
            skLineSegment(sketch, "E54.top", {"start": v(406.4, -292.1) * mm, "end": v(-406.4, -292.1) * mm});
            skLineSegment(sketch, "E54.left", {"start": v(406.4, 292.1) * mm, "end": v(406.4, -292.1) * mm});
            skLineSegment(sketch, "E54.right", {"start": v(-406.4, 292.1) * mm, "end": v(-406.4, -292.1) * mm});
            skPoint(sketch, "E54.middle", {"position": v(0, 0) * mm});
            skSolve(sketch);
        }
        {
            var Q0;
            {var subQ3=sQuery(id+"F29.wireOp",EDGE,"E54.top");Q0=makeQuery(id+"F29.imprint","IMPRINT",FACE,{"disambiguationData":[TD([[makeQuery(id+"F29.imprint","IMPRINT",EDGE,{"derivedFrom":subQ3}),-1.0]])]});}
            var Q1;
            {var subQ4=makeQuery(id+"F23.opExtrude","CAP_EDGE",EDGE,{"disambiguationData":[OSD([sQuery(id+"F22.wireOp",EDGE,"E44.MirrorCS")])],"isStart":false});Q1=makeQuery(id+"F29.imprint","IMPRINT",FACE,{"disambiguationData":[TD([[makeQuery(id+"F29.imprint","IMPRINT",EDGE,{"derivedFrom":subQ4}),-1.0]])]});}
            extrude(context, id + "F30", {"entities" : qUnion([Q0, Q1]), "depth" : 6.35 * mm});
        }
        {
            var Q0;
            Q0=makeQuery(id+"F23.opExtrude","CAP_FACE",FACE,{"disambiguationData":[OSD([sQuery(id+"F22.wireOp",EDGE,"E35.top"),sQuery(id+"F22.wireOp",EDGE,"E35.left"),sQuery(id+"F22.wireOp",EDGE,"E44.MirrorCS"),sQuery(id+"F22.wireOp",EDGE,"E45.MirrorCS")])],"isStart":true});
            var sketch = newSketch(context, id + "F31", { "sketchPlane" : qUnion([Q0])});
            skLineSegment(sketch, "E55.bottom", {"start": v(-406.4, -292.1) * mm, "end": v(406.4, -292.1) * mm});
            skLineSegment(sketch, "E55.top", {"start": v(-406.4, -177.8) * mm, "end": v(406.4, -177.8) * mm});
            skLineSegment(sketch, "E55.left", {"start": v(-406.4, -292.1) * mm, "end": v(-406.4, -177.8) * mm});
            skLineSegment(sketch, "E55.right", {"start": v(406.4, -292.1) * mm, "end": v(406.4, -177.8) * mm});
            skPoint(sketch, "E55.middle", {"position": v(0, -234.95) * mm});
            skLineSegment(sketch, "E56.MirrorCS", {"start": v(-406.4, 177.8) * mm, "end": v(406.4, 177.8) * mm});
            skLineSegment(sketch, "E57.MirrorCS", {"start": v(406.4, 292.1) * mm, "end": v(406.4, 177.8) * mm});
            skLineSegment(sketch, "E58.MirrorCS", {"start": v(-406.4, 292.1) * mm, "end": v(406.4, 292.1) * mm});
            skLineSegment(sketch, "E59.MirrorCS", {"start": v(-406.4, 292.1) * mm, "end": v(-406.4, 177.8) * mm});
            skSolve(sketch);
        }
        {
            var Q0;
            {var subQ2=sQuery(id+"F31.wireOp",EDGE,"E55.top");Q0=makeQuery(id+"F31.imprint","IMPRINT",FACE,{"disambiguationData":[TD([[makeQuery(id+"F31.imprint","IMPRINT",EDGE,{"derivedFrom":subQ2}),-1.0]])]});}
            var Q1;
            Q1=makeQuery(id+"F31.imprint","IMPRINT",FACE,{"disambiguationData":[TD([[makeQuery(id+"F31.imprint","IMPRINT",EDGE,{"derivedFrom":sQuery(id+"F31.wireOp",EDGE,"E56.MirrorCS")}),1.0]])]});
            var Q2;
            {var subQ4=makeQuery(id+"F23.opExtrude","CAP_EDGE",EDGE,{"disambiguationData":[OSD([sQuery(id+"F22.wireOp",EDGE,"E44.MirrorCS")])],"isStart":true});Q2=makeQuery(id+"F31.imprint","IMPRINT",FACE,{"disambiguationData":[TD([[makeQuery(id+"F31.imprint","IMPRINT",EDGE,{"derivedFrom":subQ4}),1.0]])]});}
            extrude(context, id + "F32", {"entities" : qUnion([Q0, Q1, Q2]), "depth" : 12.7 * mm});
        }
        {
            var Q0;
            Q0=makeQuery(id+"F24.opExtrude","CAP_FACE",FACE,{"disambiguationData":[OSD([sQuery(id+"F22.wireOp",EDGE,"E35.bottom"),sQuery(id+"F22.wireOp",EDGE,"E35.top"),sQuery(id+"F22.wireOp",EDGE,"E35.left"),sQuery(id+"F22.wireOp",EDGE,"E35.right"),sQuery(id+"F22.wireOp",EDGE,"E36"),sQuery(id+"F22.wireOp",EDGE,"E37"),sQuery(id+"F22.wireOp",EDGE,"E40.MirrorCS"),sQuery(id+"F22.wireOp",EDGE,"E41.MirrorCS"),sQuery(id+"F22.wireOp",EDGE,"E42.MirrorCS"),sQuery(id+"F22.wireOp",EDGE,"E43.MirrorCS"),sQuery(id+"F22.wireOp",EDGE,"E44.MirrorCS"),sQuery(id+"F22.wireOp",EDGE,"E45.MirrorCS")])],"isStart":false});
            var sketch = newSketch(context, id + "F33", { "sketchPlane" : qUnion([Q0])});
            skLineSegment(sketch, "E60.bottom", {"start": v(76.2, -292.1) * mm, "end": v(38.1, -292.1) * mm});
            skLineSegment(sketch, "E60.top", {"start": v(76.2, 292.1) * mm, "end": v(38.1, 292.1) * mm});
            skLineSegment(sketch, "E60.left", {"start": v(76.2, -292.1) * mm, "end": v(76.2, 292.1) * mm});
            skLineSegment(sketch, "E60.right", {"start": v(38.1, -292.1) * mm, "end": v(38.1, 292.1) * mm});
            skPoint(sketch, "E60.middle", {"position": v(57.15, 0) * mm});
            skLineSegment(sketch, "E61.MirrorCS", {"start": v(-38.1, -292.1) * mm, "end": v(-38.1, 292.1) * mm});
            skLineSegment(sketch, "E62.MirrorCS", {"start": v(-76.2, -292.1) * mm, "end": v(-76.2, 292.1) * mm});
            skSolve(sketch);
        }
        {
            var Q0;
            Q0=makeQuery(id+"F33.imprint","IMPRINT",FACE,{"disambiguationData":[TD([[makeQuery(id+"F33.imprint","IMPRINT",EDGE,{"derivedFrom":sQuery(id+"F33.wireOp",EDGE,"E60.bottom")}),-1.0]])]});
            var Q1;
            {var subQ0=sQuery(id+"F33.wireOp",EDGE,"E61.MirrorCS");Q1=makeQuery(id+"F33.imprint","IMPRINT",FACE,{"disambiguationData":[TD([[makeQuery(id+"F33.imprint","IMPRINT",EDGE,{"derivedFrom":subQ0}),1.0]])]});}
            var Q2;
            Q2=makeQuery(id+"F23.opExtrude","CAP_FACE",FACE,{"disambiguationData":[OSD([sQuery(id+"F22.wireOp",EDGE,"E35.top"),sQuery(id+"F22.wireOp",EDGE,"E35.left"),sQuery(id+"F22.wireOp",EDGE,"E44.MirrorCS"),sQuery(id+"F22.wireOp",EDGE,"E45.MirrorCS")])],"isStart":true});
            extrude(context, id + "F34", {"entities" : qUnion([Q0, Q1]), "endBound" : BoundingType.UP_TO_SURFACE, "endBoundEntityFace" : qUnion([Q2]), "depth" : 25.4 * mm});
        }
        {
            var Q0;
            Q0=makeQuery(id+"F23.opExtrude","SWEPT_FACE",FACE,{"disambiguationData":[OSD([sQuery(id+"F22.wireOp",EDGE,"E45.MirrorCS")])]});
            var sketch = newSketch(context, id + "F35", { "sketchPlane" : qUnion([Q0])});
            skLineSegment(sketch, "E63.bottom", {"start": v(-247.65, -771.53) * mm, "end": v(-285.75, -771.53) * mm});
            skLineSegment(sketch, "E63.top", {"start": v(-247.65, -835.03) * mm, "end": v(-285.75, -835.03) * mm});
            skLineSegment(sketch, "E63.left", {"start": v(-247.65, -771.53) * mm, "end": v(-247.65, -835.03) * mm});
            skLineSegment(sketch, "E63.right", {"start": v(-285.75, -771.53) * mm, "end": v(-285.75, -835.03) * mm});
            skPoint(sketch, "E63.middle", {"position": v(-266.7, -803.28) * mm});
            skSolve(sketch);
        }
        {
            var Q0;
            Q0=makeQuery(id+"F35.imprint","IMPRINT",FACE,{"disambiguationData":[TD([[makeQuery(id+"F35.imprint","IMPRINT",EDGE,{"derivedFrom":sQuery(id+"F35.wireOp",EDGE,"E63.bottom")}),1.0]])]});
            var Q1;
            Q1=makeQuery(id+"F23.opExtrude","SWEPT_FACE",FACE,{"disambiguationData":[OSD([sQuery(id+"F22.wireOp",EDGE,"E43.MirrorCS")])]});
            extrude(context, id + "F36", {"entities" : qUnion([Q0]), "endBound" : BoundingType.UP_TO_SURFACE, "endBoundEntityFace" : qUnion([Q1]), "depth" : 25.4 * mm});
        }
        {
            var Q0;
            Q0=makeQuery(id+"F25.opExtrude","SWEPT_EDGE",EDGE,{"disambiguationData":[OSD([sQuery(id+"F22.wireOp",EDGE,"E42.MirrorCS"),sQuery(id+"F22.wireOp",EDGE,"E47")])]});
            cPlane(context, id + "F37", {"entities" : qUnion([Q0]), "cplaneType" : CPlaneType.MID_PLANE, "offset" : 25.4 * mm, "width" : 152.4 * mm, "height" : 152.4 * mm});
        }
        {
            var Q0;
            Q0=makeQuery(id+"F24.opExtrude","CAP_EDGE",EDGE,{"disambiguationData":[OSD([sQuery(id+"F22.wireOp",EDGE,"E35.right")])],"isStart":false});
            cPlane(context, id + "F38", {"entities" : qUnion([Q0]), "cplaneType" : CPlaneType.MID_PLANE, "offset" : 25.4 * mm, "width" : 152.4 * mm, "height" : 152.4 * mm});
        }
        {
            var Q0;
            Q0=makeQuery(id+"F36.opExtrude","SWEPT_BODY",BODY,{"disambiguationData":[OSD([sQuery(id+"F35.wireOp",EDGE,"E63.bottom"),sQuery(id+"F35.wireOp",EDGE,"E63.top"),sQuery(id+"F35.wireOp",EDGE,"E63.left"),sQuery(id+"F35.wireOp",EDGE,"E63.right")])]});
            var Q1;
            Q1=qCreatedBy(id+"F37.planeOp",FACE);
            mirror(context, id + "F39", {"entities" : qUnion([Q0]), "mirrorPlane" : qUnion([Q1])});
        }
        {
            var Q0;
            Q0=makeQuery(id+"F39.opPattern","COPY",BODY,{"derivedFrom":makeQuery(id+"F36.opExtrude","SWEPT_BODY",BODY,{"disambiguationData":[OSD([sQuery(id+"F35.wireOp",EDGE,"E63.bottom"),sQuery(id+"F35.wireOp",EDGE,"E63.top"),sQuery(id+"F35.wireOp",EDGE,"E63.left"),sQuery(id+"F35.wireOp",EDGE,"E63.right")])]}),"instanceName":"1"});
            var Q1;
            Q1=makeQuery(id+"F36.opExtrude","SWEPT_BODY",BODY,{"disambiguationData":[OSD([sQuery(id+"F35.wireOp",EDGE,"E63.bottom"),sQuery(id+"F35.wireOp",EDGE,"E63.top"),sQuery(id+"F35.wireOp",EDGE,"E63.left"),sQuery(id+"F35.wireOp",EDGE,"E63.right")])]});
            var Q2;
            Q2=qCreatedBy(id+"F38.planeOp",FACE);
            mirror(context, id + "F40", {"entities" : qUnion([Q0, Q1]), "mirrorPlane" : qUnion([Q2])});
        }
    });
